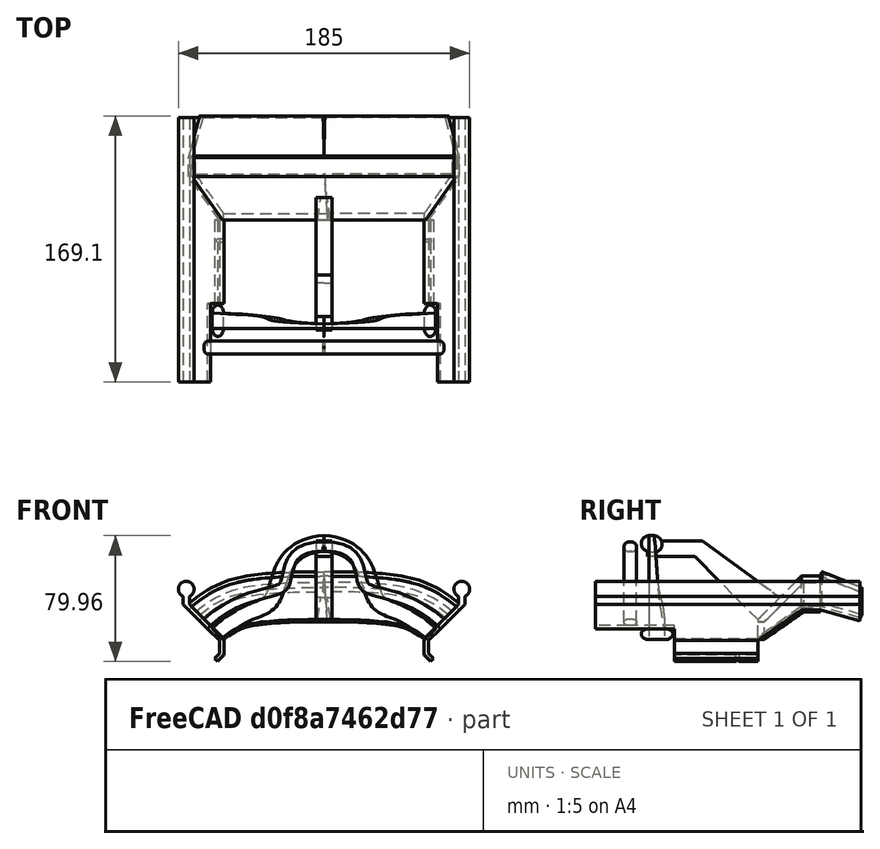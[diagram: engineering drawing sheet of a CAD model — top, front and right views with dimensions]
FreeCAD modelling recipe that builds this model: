
FCSTD DOCUMENT  (FreeCAD 0.18R16146 (Git))
Label: HeadCoil3
License: All rights reserved
LicenseURL: http://en.wikipedia.org/wiki/All_rights_reserved
objects: Sketcher::SketchObject×11, PartDesign::Plane×4, PartDesign::AdditivePipe×4, PartDesign::Pad×2, PartDesign::Body×2, PartDesign::ShapeBinder×2, Part::Mirroring×2, PartDesign::Pocket×1, App::Part×1, Part::MultiFuse×1
note: 36 computed .brp shape members not serialized (recipe doc carries the construction recipe); baked Part::Feature solids carry a one-line shape summary decoded from their .brp

FEATURE [Sketcher::SketchObject] Sketch011  label="SketchXZ-Master"
  MapMode = 5
  Placement = pos=(0,0,0) rot=(1,0,0;1.5708rad)
  Support = -> [XZ_Plane002]
  sketch-geometry (11):
    g0: LineSegment StartX=85.5 StartY=41.4174 StartZ=0 EndX=85.5 EndY=36.4174 EndZ=0
    g1: LineSegment StartX=85.5 StartY=36.4174 StartZ=0 EndX=63.4126 EndY=14.33 EndZ=0
    g2: LineSegment StartX=63.4126 StartY=14.33 StartZ=0 EndX=63.4126 EndY=4.08739 EndZ=0
    g3: LineSegment StartX=63.4126 StartY=4.08739 StartZ=0 EndX=67.5 EndY=0 EndZ=0
    g4: LineSegment StartX=67.5 StartY=0 StartZ=0 EndX=69.6213 EndY=2.12132 EndZ=0
    g5: LineSegment StartX=69.6213 StartY=2.12132 StartZ=0 EndX=66.4126 EndY=5.33003 EndZ=0
    g6: LineSegment StartX=66.4126 StartY=5.33003 StartZ=0 EndX=66.4126 EndY=13.33 EndZ=0
    g7: LineSegment StartX=66.4126 StartY=13.33 StartZ=0 EndX=89.5 EndY=36.4174 EndZ=0
    g8: LineSegment StartX=89.5 StartY=36.4174 StartZ=0 EndX=89.5 EndY=41.4174 EndZ=0
    g9: LineSegment [constr] StartX=87.5 StartY=46 StartZ=0 EndX=87.5 EndY=0 EndZ=0
    g10: ArcOfCircle CenterX=87.5 CenterY=46 CenterZ=0 NormalX=0 NormalY=0 NormalZ=1 AngleXU=0 Radius=5 StartAngle=5.12391 EndAngle=10.5841
  constraints (34):
    c: Vertical(g0)
    c: Coincident(g0,g1)
    c: Coincident(g1,g2)
    c: Vertical(g2)
    c: Coincident(g2,g3)
    c: PointOnObject(g3,g-1)
    c: Coincident(g3,g4)
    c: Coincident(g4,g5)
    c: Coincident(g5,g6)
    c: Vertical(g6)
    c: Coincident(g6,g7)
    c: Coincident(g7,g8)
    c: Vertical(g8)
    c: DistanceX(g0,g7) = 4
    c: DistanceX(g1,g6) = 3
    c: Angle(g6,g7) = 2.35619
    c: Angle(g2,g1) = 2.35619
    c: Angle(g5,g6) = 2.35619
    c: Angle(g3,g2) = 2.35619
    c: DistanceY(g0,g0) = 5
    c: Angle(g4,g3) = 1.5708
    c: Distance(g4) = 3
    c: Vertical(g9)
    c: Symmetric(g0,g8,g9)
    c: Equal(g8,g0)
    c: DistanceX(g-1,g3) = 67.5
    c: PointOnObject(g9,g-1)
    c: DistanceY(g9,g9) = 46
    c: DistanceY(g6,g6) = 8
    c: Coincident(g10,g8)
    c: Coincident(g10,g0)
    c: Radius(g10) = 5
    c: DistanceX(g-1,g10) = 87.5
    c: Coincident(g9,g10)
FEATURE [PartDesign::Plane] DatumPlane004  label="DatumPlaneSideSupportsCutouts"
  AttachmentOffset = pos=(0,0,0) rot=(1,0,0;0.785398rad)
  Length = 24.7568
  MapMode = 5
  Placement = pos=(0,0,0) rot=(0.678598,0.678598,0.281085;2.59356rad)
  ResizeMode = 0
  Support = -> [YZ_Plane002]
  Width = 33.0411
FEATURE [PartDesign::Pad] Pad002  label="PadSidePallen"
  Length = 168
  Length2 = 100
  Midplane = true
  Placement = pos=(0,0,0) rot=(1,0,0;1.5708rad)
  Profile = -> Sketch011
  Type = 0
FEATURE [Sketcher::SketchObject] Sketch012  label="SketchSideSupportCuttouts"
  ExternalGeometry = -> [Pad002]
  MapMode = 5
  Placement = pos=(0,0,0) rot=(0.678598,0.678598,0.281085;2.59356rad)
  Support = -> [DatumPlane004]
  sketch-geometry (14):
    g0: LineSegment StartX=-84 StartY=67.0371 StartZ=0 EndX=-34 EndY=67.0371 EndZ=0
    g1: LineSegment StartX=-34 StartY=67.0371 StartZ=0 EndX=-34 EndY=47.7297 EndZ=0
    g2: LineSegment StartX=-34 StartY=47.7297 StartZ=0 EndX=-84 EndY=47.7297 EndZ=0
    g3: LineSegment StartX=19 StartY=47.7297 StartZ=0 EndX=19 EndY=56.3866 EndZ=0
    g4: LineSegment StartX=19 StartY=56.3866 StartZ=0 EndX=46.6505 EndY=84.0371 EndZ=0
    g5: LineSegment StartX=46.6505 StartY=84.0371 StartZ=0 EndX=58.6505 EndY=84.0371 EndZ=0
    g6: LineSegment StartX=58.6505 StartY=84.0371 StartZ=0 EndX=84 EndY=74.0371 EndZ=0
    g7: LineSegment StartX=84 StartY=74.0371 StartZ=0 EndX=84 EndY=47.7297 EndZ=0
    g8: LineSegment StartX=84 StartY=47.7297 StartZ=0 EndX=19 EndY=47.7297 EndZ=0
    g9: LineSegment [constr] StartX=-84 StartY=89.0371 StartZ=0 EndX=-84 EndY=67.0371 EndZ=0
    g10: LineSegment [constr] StartX=46.6505 StartY=89.0371 StartZ=0 EndX=46.6505 EndY=84.0371 EndZ=0
    g11: LineSegment [constr] StartX=84 StartY=89.0371 StartZ=0 EndX=84 EndY=74.0371 EndZ=0
    g12: Circle CenterX=6 CenterY=47.7297 CenterZ=0 NormalX=0 NormalY=0 NormalZ=1 AngleXU=0 Radius=1
    g13: LineSegment StartX=-84 StartY=47.7297 StartZ=0 EndX=-84 EndY=67.0371 EndZ=0
  constraints (40):
    c: Coincident(g0,g1)
    c: Coincident(g1,g2)
    c: Horizontal(g0)
    c: Horizontal(g2)
    c: Vertical(g1)
    c: Vertical(g3)
    c: Coincident(g3,g4)
    c: Coincident(g4,g5)
    c: Horizontal(g5)
    c: Coincident(g5,g6)
    c: Coincident(g6,g7)
    c: Vertical(g7)
    c: Coincident(g7,g8)
    c: Coincident(g8,g3)
    c: Horizontal(g8)
    c: Angle(g-1,g4) = 0.785398
    c: Coincident(g-7,g9)
    c: Vertical(g9)
    c: Coincident(g0,g9)
    c: DistanceY(g9,g9) = 22
    c: PointOnObject(g10,g-7)
    c: Vertical(g10)
    c: Coincident(g4,g10)
    c: DistanceY(g10,g10) = 5
    c: Coincident(g7,g-3)
    c: Coincident(g-7,g11)
    c: PointOnObject(g11,g7)
    c: DistanceY(g11,g11) = 15
    c: Coincident(g6,g11)
    c: DistanceX(g5,g5) = 12
    c: DistanceX(g2,g2) = 50
    c: PointOnObject(g12,g-3)
    c: Radius(g12) = 1
    c: DistanceX(g2,g12) = 90
    c: PointOnObject(g3,g-6)
    c: DistanceX(g8,g8) = 65
    c: Coincident(g2,g13)
    c: Vertical(g13)
    c: Coincident(g13,g0)
    c: PointOnObject(g1,g-3)
FEATURE [PartDesign::Pocket] Pocket002
  BaseFeature = -> Pad002
  Length = 5
  Length2 = 100
  Placement = pos=(0,0,0) rot=(1,0,0;1.5708rad)
  Profile = -> Sketch012
  Reversed = true
  Type = 1
FEATURE [Sketcher::SketchObject] Sketch013  label="SketchHeadBarPath"
  MapMode = 2
  Placement = pos=(0,0,0) rot=(1,0,0;1.5708rad)
  Support = -> [XZ_Plane002]
  sketch-geometry (9):
    g0-g4: Circle [constr] x5 (B-spline internal-alignment scaffolding for g5; pole/knot coordinates omitted)
    g5: BSplineCurve PolesCount=5 KnotsCount=3 Degree=3 IsPeriodic=0
    g6: GeomPoint [constr] X=85 Y=35 Z=0
    g7: GeomPoint [constr] X=37.75 Y=53.75 Z=0
    g8: GeomPoint [constr] X=0 Y=55 Z=0
  constraints (16):
    c: Radius(g0) = 1
    c: Equal(g0, g1-g4) x4
    c: PointOnObject(g4,g-2)
    c: InternalAlignment(g0-g4 -> g5) x5
    c: InternalAlignment(g6,g5)
    c: InternalAlignment(g7,g5)
    c: InternalAlignment(g8,g5)
    c: DistanceY(g-1,g4) = 55
    c: DistanceY(g-1,g3) = 55
    c: DistanceY(g-1,g2) = 55
    c: DistanceY(g-1,g1) = 50
    c: DistanceX(g-1,g3) = 13
    c: DistanceX(g-1,g2) = 35
    c: DistanceX(g-1,g1) = 68
    c: DistanceY(g-1,g0) = 35
    c: DistanceX(g-1,g0) = 85
FEATURE [PartDesign::Plane] DatumPlane005  label="DatumPlaneSidePannel"
  Length = 33.0411
  MapMode = 5
  Placement = pos=(24.5413,2.5463e-12,-24.5413) rot=(-0.382683,0,0.92388;3.14159rad)
  ResizeMode = 0
  Support = -> [Pocket002]
  Width = 24.7568
FEATURE [Sketcher::SketchObject] Sketch015  label="SketchNoseBarProfile"
  ExternalGeometry = -> [Pocket002]
  MapMode = 5
  Placement = pos=(24.5413,2.5463e-12,-24.5413) rot=(-0.382683,0,0.92388;3.14159rad)
  Support = -> [DatumPlane005]
  sketch-geometry (4):
    g0: ArcOfCircle CenterX=-70.0371 CenterY=63 CenterZ=0 NormalX=0 NormalY=0 NormalZ=1 AngleXU=0 Radius=3 StartAngle=0 EndAngle=3.14159
    g1: ArcOfCircle CenterX=-70.0371 CenterY=61 CenterZ=0 NormalX=0 NormalY=0 NormalZ=1 AngleXU=0 Radius=3 StartAngle=3.14159 EndAngle=6.28319
    g2: LineSegment StartX=-73.0371 StartY=63 StartZ=0 EndX=-73.0371 EndY=61 EndZ=0
    g3: LineSegment StartX=-67.0371 StartY=63 StartZ=0 EndX=-67.0371 EndY=61 EndZ=0
  constraints (10):
    c: Tangent(g0,g3) = 1.5708
    c: Tangent(g0,g2) = -1.5708
    c: Tangent(g2,g1) = -1.5708
    c: Tangent(g3,g1) = 1.5708
    c: Vertical(g2)
    c: Equal(g0,g1)
    c: Radius(g0) = 3
    c: DistanceY(g3,g3) = 2
    c: PointOnObject(g1,g-3)
    c: DistanceY(g0,g-3) = 21
FEATURE [Sketcher::SketchObject] Sketch016  label="SketchHeadBarProfile"
  ExternalGeometry = -> [Sketch012]
  MapMode = 5
  Placement = pos=(24.5413,2.5463e-12,-24.5413) rot=(-0.382683,0,0.92388;3.14159rad)
  Support = -> [DatumPlane005]
  sketch-geometry (4):
    g0: LineSegment StartX=-86.8278 StartY=-59.7514 StartZ=0 EndX=-76.8278 EndY=-85.1009 EndZ=0
    g1: LineSegment StartX=-76.8278 StartY=-85.1009 StartZ=0 EndX=-74.0371 EndY=-84 EndZ=0
    g2: LineSegment StartX=-74.0371 StartY=-84 StartZ=0 EndX=-84.0371 EndY=-58.6505 EndZ=0
    g3: LineSegment StartX=-84.0371 StartY=-58.6505 StartZ=0 EndX=-86.8278 EndY=-59.7514 EndZ=0
  constraints (10):
    c: Coincident(g0,g1)
    c: Coincident(g1,g2)
    c: Coincident(g2,g3)
    c: Coincident(g3,g0)
    c: Equal(g0,g2)
    c: Parallel(g0,g2)
    c: Perpendicular(g3,g2)
    c: Distance(g1) = 3
    c: Coincident(g2,g-4)
    c: Coincident(g1,g-3)
FEATURE [Sketcher::SketchObject] Sketch017  label="SketchNoseBarPath"
  MapMode = 5
  Placement = pos=(0,0,0) rot=(1,0,0;1.5708rad)
  Support = -> [XZ_Plane002]
  sketch-geometry (9):
    g0-g4: Circle [constr] x5 (B-spline internal-alignment scaffolding for g5; pole/knot coordinates omitted)
    g5: BSplineCurve PolesCount=5 KnotsCount=3 Degree=3 IsPeriodic=0
    g6: GeomPoint [constr] X=-0.960096 Y=70.0062 Z=0
    g7: GeomPoint [constr] X=23.75 Y=46.002 Z=0
    g8: GeomPoint [constr] X=71.8527 Y=23.1682 Z=0
  constraints (6):
    c: Radius(g0) = 3
    c: Equal(g0, g1-g4) x4
    c: InternalAlignment(g0-g4 -> g5) x5
    c: InternalAlignment(g6,g5)
    c: InternalAlignment(g7,g5)
    c: InternalAlignment(g8,g5)
FEATURE [PartDesign::AdditivePipe] AdditivePipe003
  AuxilleryCurvelinear = true
  AuxillerySpineTangent = false
  BaseFeature = -> Pocket002
  Binormal = (0,0,0)
  Mode = 0
  Placement = pos=(0,0,0) rot=(1,0,0;1.5708rad)
  Profile = -> Sketch016
  Spine = -> Sketch013 [Edge1]
  SpineTangent = false
  Transformation = 0
  Transition = 0
FEATURE [PartDesign::AdditivePipe] AdditivePipe004
  AuxilleryCurvelinear = true
  AuxillerySpineTangent = false
  BaseFeature = -> AdditivePipe003
  Binormal = (0,0,0)
  Mode = 0
  Placement = pos=(0,0,0) rot=(1,0,0;1.5708rad)
  Profile = -> Sketch015
  Spine = -> Sketch017 [Edge1]
  SpineTangent = false
  Transformation = 0
  Transition = 0
FEATURE [PartDesign::Body] Body001  label="BodyMirrorMount"
  Group = -> [Sketch011,DatumPlane004,Pad002,Sketch012,Pocket002,Sketch013,DatumPlane005,Sketch015,Sketch016,Sketch017,AdditivePipe003,AdditivePipe004]
  Origin = -> Origin002
  Tip = -> AdditivePipe004
FEATURE [PartDesign::ShapeBinder] CopyAdditivePipe004
  Placement = pos=(0,0,0) rot=(1,0,0;1.5708rad)
  TraceSupport = false
FEATURE [PartDesign::Plane] DatumPlane
  Length = 33.0411
  MapMode = 5
  Placement = pos=(24.5413,2.5954e-12,-24.5413) rot=(-0.382683,0,0.92388;3.14159rad)
  ResizeMode = 0
  Support = -> [CopyAdditivePipe004]
  Width = 24.7568
FEATURE [Sketcher::SketchObject] Sketch
  ExternalGeometry = -> [CopyAdditivePipe004]
  MapMode = 5
  Placement = pos=(24.5413,2.5954e-12,-24.5413) rot=(-0.382683,0,0.92388;3.14159rad)
  Support = -> [DatumPlane]
  sketch-geometry (8):
    g0: LineSegment StartX=-56.3866 StartY=-19 StartZ=0 EndX=-54.9723 EndY=-19 EndZ=0
    g1: LineSegment StartX=-54.9723 StartY=-19 StartZ=0 EndX=-54.9723 EndY=-23.2426 EndZ=0
    g2: LineSegment StartX=-54.9723 StartY=-23.2426 StartZ=0 EndX=-80.0371 EndY=-48.3074 EndZ=0
    g3: LineSegment StartX=-80.0371 StartY=-48.3074 StartZ=0 EndX=-80.0371 EndY=-58.6505 EndZ=0
    g4: LineSegment StartX=-80.0371 StartY=-58.6505 StartZ=0 EndX=-84.0371 EndY=-58.6505 EndZ=0
    g5: LineSegment StartX=-84.0371 StartY=-58.6505 StartZ=0 EndX=-84.0371 EndY=-46.6505 EndZ=0
    g6: LineSegment StartX=-84.0371 StartY=-46.6505 StartZ=0 EndX=-56.3866 EndY=-19 EndZ=0
    g7: LineSegment [constr] StartX=-80.0371 StartY=-48.3074 StartZ=0 EndX=-82.8655 EndY=-45.4789 EndZ=0
  constraints (23):
    c: Horizontal(g0)
    c: Coincident(g0,g1)
    c: Vertical(g1)
    c: Coincident(g1,g2)
    c: Coincident(g2,g3)
    c: Coincident(g3,g4)
    c: Horizontal(g4)
    c: Coincident(g4,g5)
    c: Vertical(g5)
    c: Coincident(g5,g6)
    c: PointOnObject(g6,g0)
    c: Parallel(g6,g2)
    c: Coincident(g6,g0)
    c: Parallel(g3,g5)
    c: Coincident(g5,g-5)
    c: Coincident(g4,g-5)
    c: Coincident(g0,g-4)
    c: Coincident(g0,g-4)
    c: Coincident(g7,g2)
    c: PointOnObject(g7,g6)
    c: Perpendicular(g6,g7)
    c: DistanceX(g4,g4) = 4
    c: Distance(g7) = 4
FEATURE [PartDesign::ShapeBinder] ShapeBinder
  Placement = pos=(0,0,0) rot=(1,0,0;1.5708rad)
  Support = -> [Sketch013]
  TraceSupport = false
FEATURE [PartDesign::AdditivePipe] AdditivePipe
  AuxilleryCurvelinear = true
  AuxillerySpineTangent = false
  Binormal = (0,0,0)
  Mode = 0
  Placement = pos=(24.5413,2.595e-12,-24.5413) rot=(-0.382683,0,0.92388;3.14159rad)
  Profile = -> Sketch
  Spine = -> ShapeBinder [Edge1]
  SpineTangent = false
  Transformation = 0
  Transition = 0
FEATURE [Sketcher::SketchObject] Sketch018
  ExternalGeometry = -> [AdditivePipe]
  MapMode = 5
  Placement = pos=(0,0,0) rot=(0.57735,0.57735,0.57735;2.0944rad)
  Support = -> [YZ_Plane003]
  sketch-geometry (6):
    g0: LineSegment StartX=-51 StartY=76.6466 StartZ=0 EndX=-16 EndY=76.6466 EndZ=0
    g1: LineSegment StartX=-16 StartY=76.6466 StartZ=0 EndX=33.1595 EndY=40.7713 EndZ=0
    g2: LineSegment StartX=33.1595 StartY=40.7713 StartZ=0 EndX=19 EndY=26.6466 EndZ=0
    g3: LineSegment StartX=19 StartY=26.6466 StartZ=0 EndX=-21 EndY=66.6466 EndZ=0
    g4: LineSegment StartX=-21 StartY=66.6466 StartZ=0 EndX=-51 EndY=66.6466 EndZ=0
    g5: LineSegment StartX=-51 StartY=66.6466 StartZ=0 EndX=-51 EndY=76.6466 EndZ=0
  constraints (17):
    c: Horizontal(g0)
    c: Coincident(g0,g1)
    c: Coincident(g1,g2)
    c: Coincident(g2,g3)
    c: Coincident(g3,g4)
    c: Horizontal(g4)
    c: Coincident(g4,g5)
    c: Vertical(g5)
    c: Coincident(g5,g0)
    c: Angle(g3,g-1) = 0.785398
    c: Coincident(g2,g-3)
    c: PointOnObject(g1,g-3)
    c: DistanceY(g5,g5) = 10
    c: DistanceX(g0,g0) = 35
    c: Distance(g2) = 20
    c: DistanceX(g4,g2) = 70
    c: DistanceY(g2,g4) = 40
FEATURE [PartDesign::Pad] Pad
  BaseFeature = -> AdditivePipe
  Length = 5
  Length2 = 100
  Placement = pos=(24.5413,2.595e-12,-24.5413) rot=(-0.382683,0,0.92388;3.14159rad)
  Profile = -> Sketch018
  Type = 0
FEATURE [PartDesign::Plane] DatumPlane006
  AttachmentOffset = pos=(0,0,56) rot=(0,0,1;0rad)
  Length = 24
  MapMode = 5
  Placement = pos=(0,-56,-5.7727e-12) rot=(1,0,0;1.5708rad)
  ResizeMode = 0
  Support = -> [XZ_Plane003]
  Width = 24
FEATURE [Sketcher::SketchObject] Sketch019
  ExternalGeometry = -> [Pad]
  MapMode = 5
  Placement = pos=(0,-56,-5.7727e-12) rot=(1,0,0;1.5708rad)
  Support = -> [DatumPlane006]
  sketch-geometry (12):
    g0: LineSegment StartX=5 StartY=66.6466 StartZ=0 EndX=5 EndY=76.6466 EndZ=0
    g1-g6: Circle [constr] x6 (B-spline internal-alignment scaffolding for g7; pole/knot coordinates omitted)
    g7: BSplineCurve PolesCount=6 KnotsCount=4 Degree=3 IsPeriodic=0
    g8-g11: GeomPoint [constr] x4 (B-spline internal-alignment scaffolding for g7; pole/knot coordinates omitted)
  constraints (6):
    c: Vertical(g0)
    c: PointOnObject(g1,g-2)
    c: Radius(g1) = 3
    c: Equal(g1, g2-g6) x5
    c: InternalAlignment(g1-g6 -> g7) x6
    c: InternalAlignment(g8-g11 -> g7) x4
FEATURE [Sketcher::SketchObject] Sketch020
  MapMode = 5
  Placement = pos=(0,0,0) rot=(0.57735,0.57735,0.57735;2.0944rad)
  Support = -> [YZ_Plane003]
  sketch-geometry (4):
    g0: ArcOfCircle CenterX=-49.9996 CenterY=74.9593 CenterZ=0 NormalX=0 NormalY=0 NormalZ=1 AngleXU=0 Radius=5 StartAngle=1.5708 EndAngle=4.71239
    g1: ArcOfCircle CenterX=-46.9996 CenterY=74.9593 CenterZ=0 NormalX=0 NormalY=0 NormalZ=1 AngleXU=0 Radius=5 StartAngle=4.71239 EndAngle=7.85398
    g2: LineSegment StartX=-49.9996 StartY=69.9593 StartZ=0 EndX=-46.9996 EndY=69.9593 EndZ=0
    g3: LineSegment StartX=-49.9996 StartY=79.9593 StartZ=0 EndX=-46.9996 EndY=79.9593 EndZ=0
  constraints (8):
    c: Tangent(g0,g3) = 1.5708
    c: Tangent(g0,g2) = -1.5708
    c: Tangent(g2,g1) = -1.5708
    c: Tangent(g3,g1) = 1.5708
    c: Horizontal(g2)
    c: Equal(g0,g1)
    c: Radius(g1) = 5
    c: DistanceX(g2,g2) = 3
FEATURE [Sketcher::SketchObject] Sketch021
  MapMode = 5
  Placement = pos=(24.5413,2.5954e-12,-24.5413) rot=(-0.382683,0,0.92388;3.14159rad)
  Support = -> [DatumPlane]
  sketch-geometry (4):
    g0: ArcOfCircle CenterX=-60 CenterY=50 CenterZ=0 NormalX=0 NormalY=0 NormalZ=1 AngleXU=0 Radius=5 StartAngle=0 EndAngle=3.14159
    g1: ArcOfCircle CenterX=-60 CenterY=40 CenterZ=0 NormalX=0 NormalY=0 NormalZ=1 AngleXU=0 Radius=5 StartAngle=3.14159 EndAngle=6.28319
    g2: LineSegment StartX=-65 StartY=50 StartZ=0 EndX=-65 EndY=40 EndZ=0
    g3: LineSegment StartX=-55 StartY=50 StartZ=0 EndX=-55 EndY=40 EndZ=0
  constraints (10):
    c: Tangent(g0,g3) = 1.5708
    c: Tangent(g0,g2) = -1.5708
    c: Tangent(g2,g1) = -1.5708
    c: Tangent(g3,g1) = 1.5708
    c: Vertical(g2)
    c: Equal(g0,g1)
    c: Radius(g0) = 5
    c: DistanceY(g3,g3) = 10
    c: DistanceX(g0,g-1) = 60
    c: DistanceY(g-1,g1) = 40
FEATURE [PartDesign::AdditivePipe] AdditivePipe005
  AuxilleryCurvelinear = true
  AuxillerySpineTangent = false
  BaseFeature = -> Pad
  Binormal = (0,0,0)
  Mode = 0
  Placement = pos=(24.5413,2.595e-12,-24.5413) rot=(-0.382683,0,0.92388;3.14159rad)
  Profile = -> Sketch021
  Sections = -> [Sketch020]
  Spine = -> Sketch019 [Edge2]
  SpineTangent = false
  Transformation = 1
  Transition = 0
FEATURE [PartDesign::Body] Body002  label="HeadCoil"
  Group = -> [DatumPlane,CopyAdditivePipe004,Sketch,ShapeBinder,AdditivePipe,Sketch018,Pad,DatumPlane006,Sketch019,Sketch020,Sketch021,AdditivePipe005]
  Origin = -> Origin003
  Tip = -> AdditivePipe005
FEATURE [App::Part] Part
  Group = -> [Body001,Body002]
  License = CC BY 3.0
  LicenseURL = http://creativecommons.org/licenses/by/3.0/
  Origin = -> Origin001
FEATURE [Part::Mirroring] Part__Mirroring  label="AdditivePipe005 (Mirror #1)"
  Base = (0,0,0)
  Normal = (1,0,0)
  Source = -> AdditivePipe005
FEATURE [Part::Mirroring] Part__Mirroring001  label="AdditivePipe004 (Mirror #2)"
  Base = (0,0,0)
  Normal = (1,0,0)
  Source = -> AdditivePipe004
FEATURE [Part::MultiFuse] Fusion
  Shapes = -> [Part__Mirroring,AdditivePipe005,Part__Mirroring001,AdditivePipe004,Body002,Body001]
